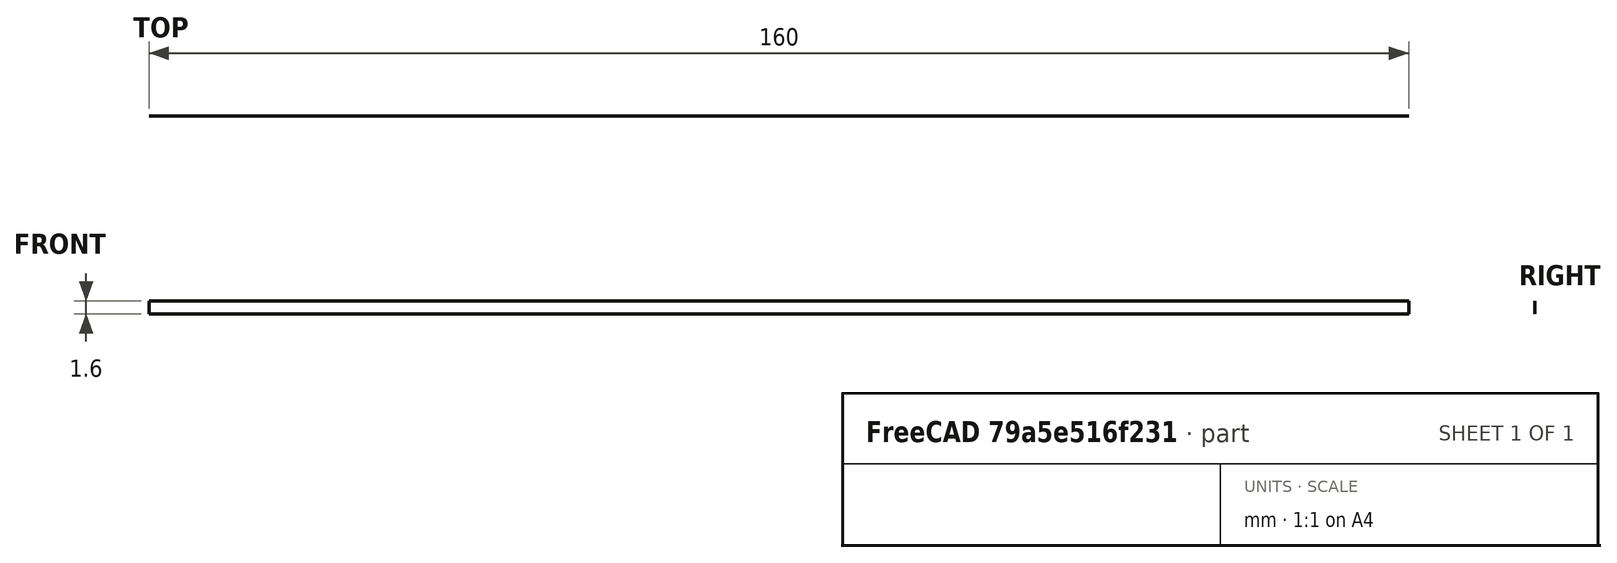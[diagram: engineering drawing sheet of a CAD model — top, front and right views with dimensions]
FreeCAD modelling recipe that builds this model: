
FCSTD DOCUMENT  (FreeCAD 0.21R33675 (Git))
Label: spacings
License: All rights reserved
LicenseURL: https://en.wikipedia.org/wiki/All_rights_reserved
objects: Part::Part2DObjectPython×2, Part::Mirroring×1
note: 3 computed .brp shape members not serialized (recipe doc carries the construction recipe); baked Part::Feature solids carry a one-line shape summary decoded from their .brp

FEATURE [Part::Part2DObjectPython] Rectangle  # Draft 2D object (typed FeaturePython)
  Area = 256
  ChamferSize = 0
  Columns = 1
  FilletRadius = 0
  Height = 160
  Length = -1.6
  MakeFace = true
  Placement = pos=(0,0,0) rot=(1,-1e-06,1e-06;1.5708rad)
  Rows = 1
FEATURE [Part::Part2DObjectPython] Rectangle001  # Draft 2D object (typed FeaturePython)
  Area = 256
  ChamferSize = 0
  Columns = 1
  FilletRadius = 0
  Height = 160
  Length = -1.6
  MakeFace = true
  Placement = pos=(0,0,0) rot=(0.577349,-0.577351,0.577351;2.0944rad)
  Rows = 1
FEATURE [Part::Mirroring] Mirror  label="Rectangle001 (mirrored)"
  Base = (0,0,0)
  Normal = (-1,1.19867e-09,-2.10734e-06)
  Source = -> Rectangle001
